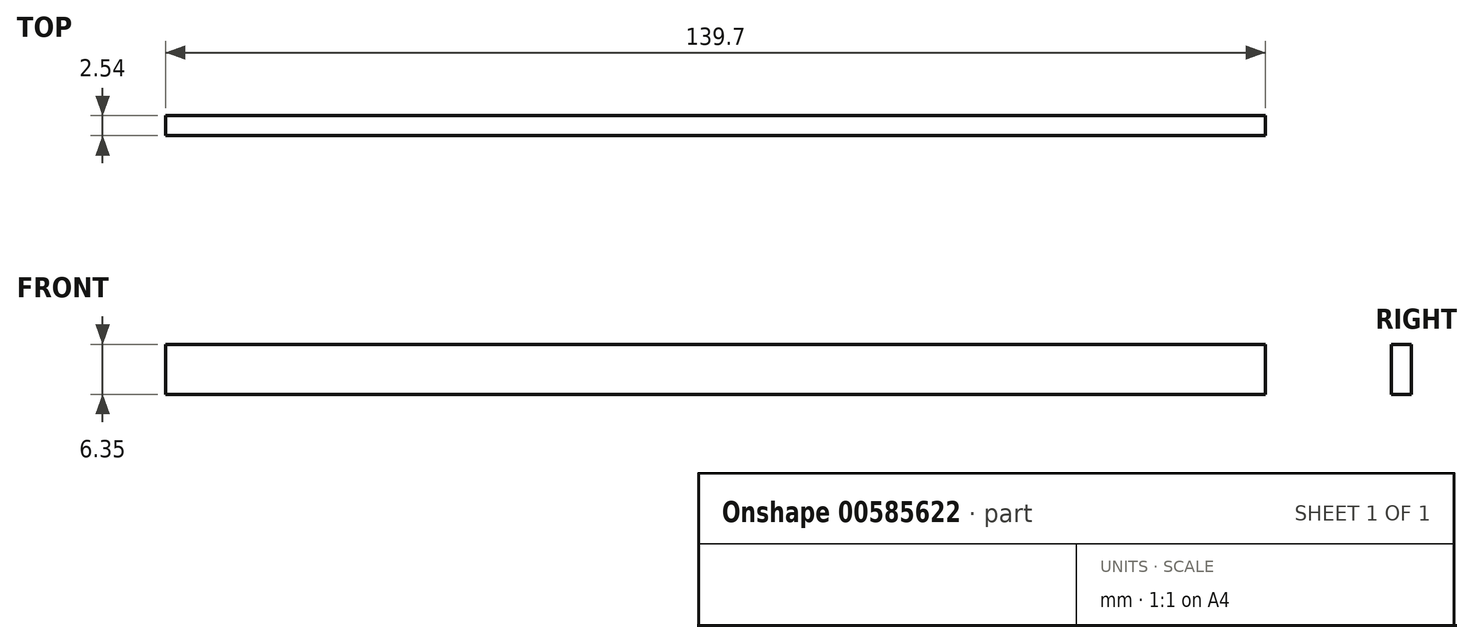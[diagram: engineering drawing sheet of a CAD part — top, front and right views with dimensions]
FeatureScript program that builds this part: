
annotation { "Feature Type Name" : "Feature", "Feature Type Description" : "" }
export const myFeature = defineFeature(function(context is Context, id is Id, definition is map)
    precondition{}
    {
        {
            var Q0;
            Q0=qCreatedBy(makeId("Top.planeOp"),FACE);
            var sketch = newSketch(context, id + "F0", { "sketchPlane" : qUnion([Q0])});
            skLineSegment(sketch, "E0.bottom", {"start": v(-69.85, 1.27) * mm, "end": v(69.85, 1.27) * mm});
            skLineSegment(sketch, "E0.top", {"start": v(-69.85, -1.27) * mm, "end": v(69.85, -1.27) * mm});
            skLineSegment(sketch, "E0.left", {"start": v(-69.85, 1.27) * mm, "end": v(-69.85, -1.27) * mm});
            skLineSegment(sketch, "E0.right", {"start": v(69.85, 1.27) * mm, "end": v(69.85, -1.27) * mm});
            skPoint(sketch, "E0.middle", {"position": v(0, 0) * mm});
            skSolve(sketch);
        }
        {
            var Q0;
            Q0 = qSketchRegion(id + "F0", true);
            extrude(context, id + "F1", {"entities" : qUnion([Q0]), "depth" : 6.35 * mm, "offsetDistance" : 25.4 * mm});
        }
    });
